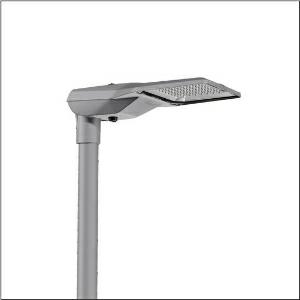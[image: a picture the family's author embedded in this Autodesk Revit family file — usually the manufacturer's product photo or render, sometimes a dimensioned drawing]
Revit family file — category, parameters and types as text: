
# Revit family: streetlight_sl_21_midi___p0_8ab_5xe3r33t08nb_adf9
name_source: partatom
category: Lighting Fixtures
units: mm (PartAtom-declared; Revit-internal decimal feet)

## family parameters
Cut with Voids When Loaded = No
Host = Face
Light Source = No
Part Type = Normal
Room Calculation Point = No
Round Connector Dimension = Use Diameter
Shared = No

## types (1)
- --- (1 x LED, 19710 lm, 151.2 W, 3000K)
    Apparent Load = 151 VA
    CIE Flux Codes = 39 72 97 100 100
    Color Rendering = 70
    Color Temperature = 3000K
    Default Elevation = 1800 mm
    Description = Streetlight SL 21 midi, mast luminaire, primary light control with lens, of PMMA, primary optical cover: cover, of toughened safety glass, transparent, light distribution: P0.8aB, light emission: direct distribution, primary light characteristic: asymmetric, installation type: post-top, side-entry, LED, High Power LED, rated luminous flux: 19.710lm, luminous efficacy: 130lm/W, light colour: 730, colour temperature: 3000K, control gear: D4i, control: pre-setting: logarithmic dimming characteristic, flexible luminous flux parameterisation, time-dependent luminous flux control, constant luminous flux control, overheat protection, mains connection: 230..240V, AC, 50/60Hz, start of lifetime: 151W, end of service life: 157W, reduction: 70W, luminaire housing, of diecast aluminium, powder-coated, SITECO metallic grey (DB 702S), corrosivity category C5 high according to DIN EN ISO 12944, multi-level sealing system, sealing non-destructively replaceable, inclination adjustable: 0°, 5°, 10°, 15°, please order mast flange separately, length: 644mm, width: 335mm, height: 110mm, mast flange for spigot size: 42mm (side-entry): 5XC10008XM4, 60/48mm (side-entry/post-top): 5XC10108XM2, 76/60mm (side-entry/post-top): 5XC10108XM1, mounting height: 4..8m, Smart Interface below and above, protection rating (complete): IP66, insulation class (complete): insulation class II (safety insulation), certification: CE, ENEC, ENEC+, VDE, impact resistance: IK10, permissible operating ambient temperature for outdoor applications: -40..+50°C, standard-compliant lighting for roads and squares, packaging unit: 1 piece

Light Distribution: P0.8aB
    Height = 111 mm
    Lamp = 1 x LED
    Lamp Light Flux = 19710 lm
    Lamp Power = 151.2 W
    Lamp count = 1
    Length = 644 mm
    Luminous efficacy = 130 lm/W
    Manufacturer = Siteco
    ModVariant = No
    Model = 5XE3R33T08NB
    Number of Poles = 1
    OnlyDefault = Yes
    Power Factor = 1
    Product Name = Streetlight SL 21 midi | P0.8aB
    Product group = mast luminaire | pylon top
    ProductGroupID = 6100
    Protection Class = Protection class II
    Protection Degree = IP 66
    RLX_Detail_Level = 1
    RLX_Emergency_Light_Flux = 0 lm
    RLX_Emergency_Type = 0
    RLX_Emergency_Type_DB = No
    RlxData = <blob elided: 90733 chars, md5=18688d47>
    Socket = socket
    Standby Power = 0 W
    System Light Flux = 19710 lm
    System Power = 151 W
    Type Comments = factory setting: luminous flux: 100 % | dim-lin: 254 | 802 mA
    Type Image = l_1004304.jpg
    URL = http://relux.com
    VarID = @adj_078645
    Voltage = 0 V
    Weight = 0.00 kg
    Width = 336 mm

## geometry (parser evidence)
native form markers: Blend x4, Sweep x10
no freeform markers — native parametric forms only
